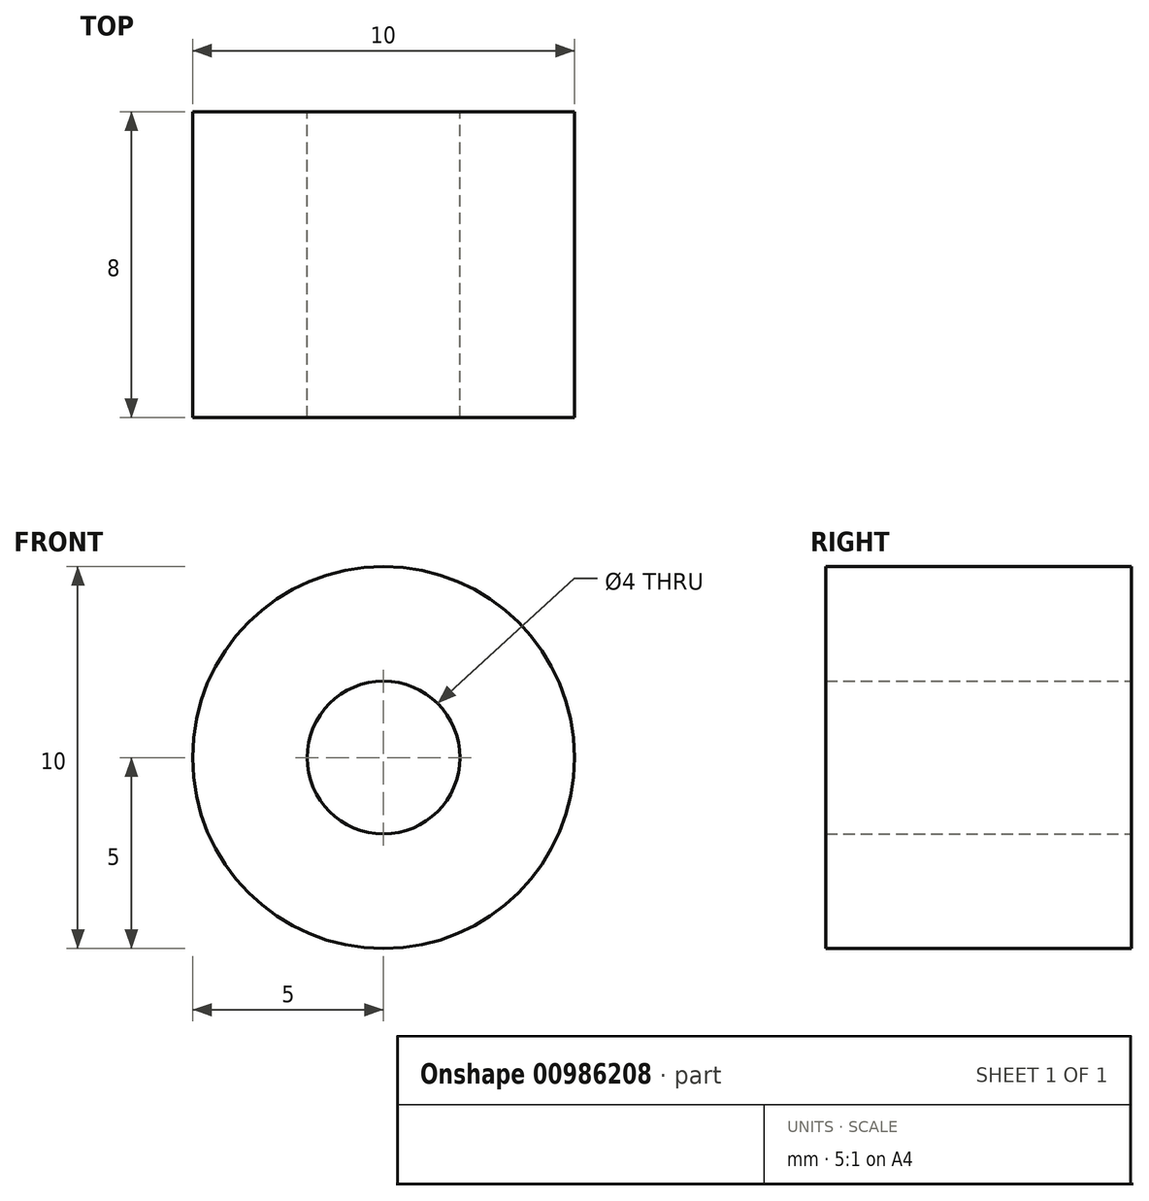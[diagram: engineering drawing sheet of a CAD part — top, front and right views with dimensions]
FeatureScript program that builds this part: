
annotation { "Feature Type Name" : "Feature", "Feature Type Description" : "" }
export const myFeature = defineFeature(function(context is Context, id is Id, definition is map)
    precondition{}
    {
        {
            var Q0;
            Q0=qCreatedBy(makeId("Front.planeOp"),FACE);
            var sketch = newSketch(context, id + "F0", { "sketchPlane" : qUnion([Q0])});
            skCircle(sketch, "E0", {"center": v(0, 0) * mm, "radius": 2 * mm});
            skCircle(sketch, "E1", {"center": v(0, 0) * mm, "radius": 5 * mm});
            skSolve(sketch);
        }
        {
            var Q0;
            Q0=makeQuery(id+"F0.imprint","IMPRINT",FACE,{"disambiguationData":[TD([[makeQuery(id+"F0.imprint","IMPRINT",EDGE,{"derivedFrom":sQuery(id+"F0.wireOp",EDGE,"E0")}),-1.0]])]});
            extrude(context, id + "F1", {"entities" : qUnion([Q0]), "depth" : 8 * mm, "offsetDistance" : 25 * mm});
        }
    });
